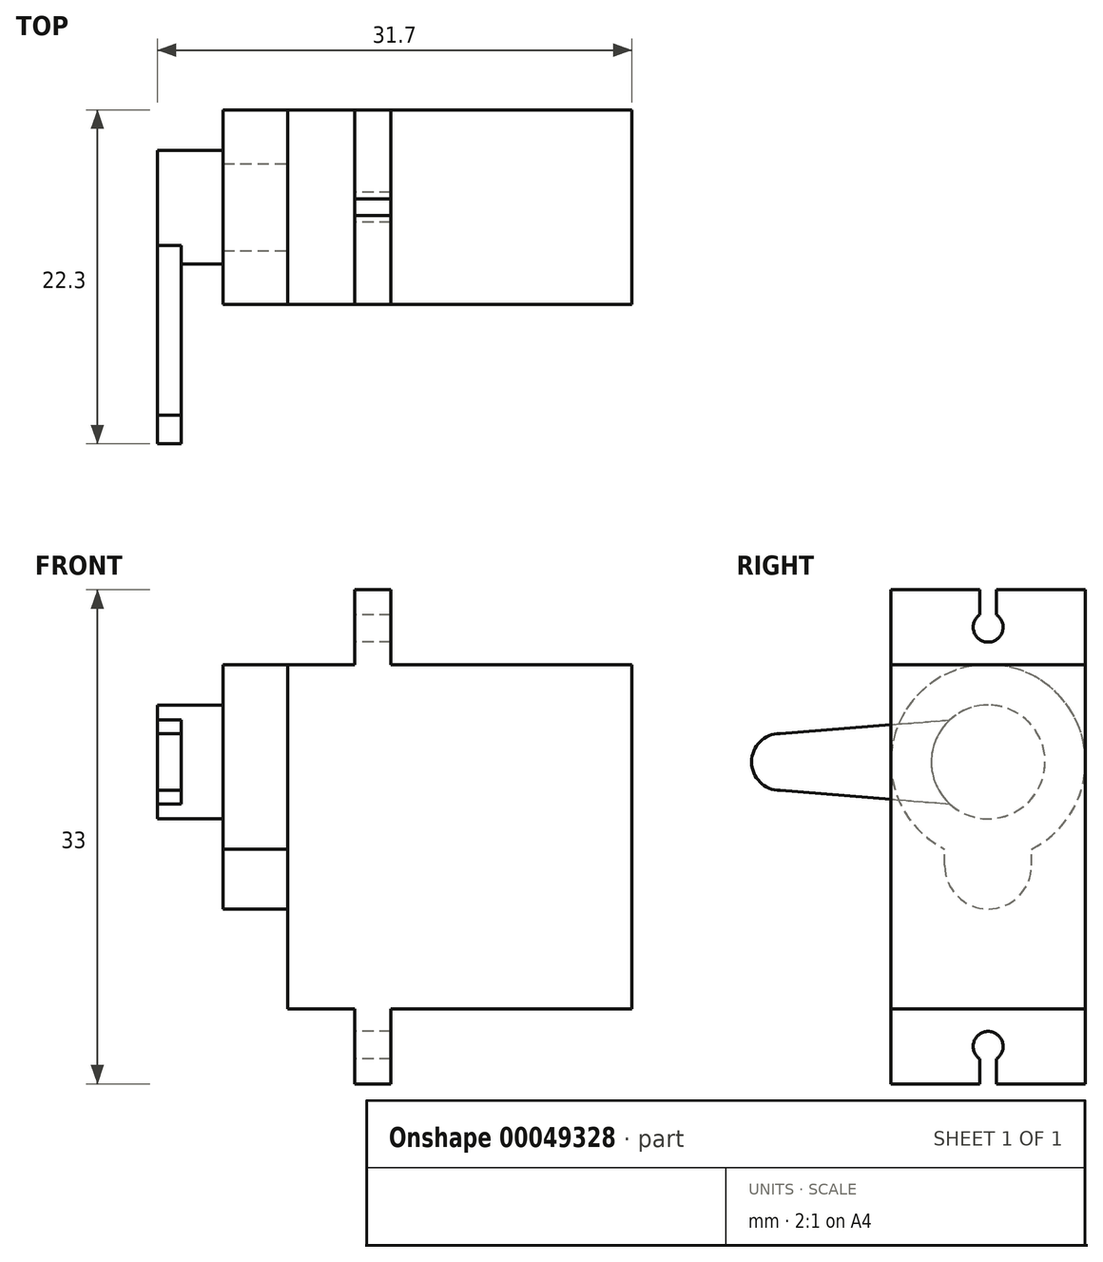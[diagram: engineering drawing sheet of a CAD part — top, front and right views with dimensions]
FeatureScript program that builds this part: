
annotation { "Feature Type Name" : "Feature", "Feature Type Description" : "" }
export const myFeature = defineFeature(function(context is Context, id is Id, definition is map)
    precondition{}
    {
        {
            var Q0;
            Q0=qCreatedBy(makeId("Front.planeOp"),FACE);
            var sketch = newSketch(context, id + "F0", { "sketchPlane" : qUnion([Q0])});
            skLineSegment(sketch, "E0.bottom", {"start": v(-23, 11.5) * mm, "end": v(0, 11.5) * mm});
            skLineSegment(sketch, "E0.top", {"start": v(-23, -11.5) * mm, "end": v(0, -11.5) * mm});
            skLineSegment(sketch, "E0.left", {"start": v(-23, 11.5) * mm, "end": v(-23, -11.5) * mm});
            skLineSegment(sketch, "E0.right", {"start": v(0, 11.5) * mm, "end": v(0, -11.5) * mm});
            skLineSegment(sketch, "E1.bottom", {"start": v(-18.5, 16.5) * mm, "end": v(-16.1, 16.5) * mm});
            skLineSegment(sketch, "E1.top", {"start": v(-18.5, -16.5) * mm, "end": v(-16.1, -16.5) * mm});
            skLineSegment(sketch, "E1.left", {"start": v(-18.5, 16.5) * mm, "end": v(-18.5, -16.5) * mm});
            skLineSegment(sketch, "E1.right", {"start": v(-16.1, 16.5) * mm, "end": v(-16.1, -16.5) * mm});
            skLineSegment(sketch, "E2", {"start": v(-23, 0) * mm, "end": v(0, 0) * mm, "construction": true});
            skSolve(sketch);
        }
        {
            var Q0;
            {var subQ5=sQuery(id+"F0.wireOp",EDGE,"E0.left");Q0=makeQuery(id+"F0.imprint","IMPRINT",FACE,{"disambiguationData":[TD([[makeQuery(id+"F0.imprint","IMPRINT",EDGE,{"derivedFrom":subQ5}),1.0]])]});}
            var Q1;
            {var subQ3=sQuery(id+"F0.wireOp",EDGE,"E1.bottom");Q1=makeQuery(id+"F0.imprint","IMPRINT",FACE,{"disambiguationData":[TD([[makeQuery(id+"F0.imprint","IMPRINT",EDGE,{"derivedFrom":subQ3}),-1.0]])]});}
            var Q2;
            {var subQ5=sQuery(id+"F0.wireOp",EDGE,"E0.right");Q2=makeQuery(id+"F0.imprint","IMPRINT",FACE,{"disambiguationData":[TD([[makeQuery(id+"F0.imprint","IMPRINT",EDGE,{"derivedFrom":subQ5}),-1.0]])]});}
            var Q3;
            {var subQ3=sQuery(id+"F0.wireOp",EDGE,"E1.top");Q3=makeQuery(id+"F0.imprint","IMPRINT",FACE,{"disambiguationData":[TD([[makeQuery(id+"F0.imprint","IMPRINT",EDGE,{"derivedFrom":subQ3}),1.0]])]});}
            var Q4;
            {var subQ3=sQuery(id+"F0.wireOp",EDGE,"E0.bottom");var subQ5=sQuery(id+"F0.wireOp",EDGE,"E1.left");var subQ7=makeQuery(id+"F0.imprint","INTERSECT",VERTEX,{"derivedFrom":[subQ3,subQ5]});Q4=makeQuery(id+"F0.imprint","IMPRINT",FACE,{"disambiguationData":[TD([[makeQuery(id+"F0.imprint","IMPRINT",EDGE,{"disambiguationData":[TD([[subQ7,-1.0]])],"derivedFrom":subQ3}),-1.0]])]});}
            extrude(context, id + "F1", {"entities" : qUnion([Q0, Q1, Q2, Q3, Q4]), "depth" : 13 * mm});
        }
        {
            var Q0;
            Q0=makeQuery(id+"F1.opExtrude","SWEPT_FACE",FACE,{"disambiguationData":[OSD([sQuery(id+"F0.wireOp",EDGE,"E0.left")])]});
            var sketch = newSketch(context, id + "F2", { "sketchPlane" : qUnion([Q0])});
            skLineSegment(sketch, "E3", {"start": v(6.5, 11.5) * mm, "end": v(6.5, -11.5) * mm, "construction": true});
            skArc(sketch, "E4", {"start": v(9.4, -0.82) * mm, "mid": v(6.5, 11.5) * mm, "end": v(3.6, -0.82) * mm});
            skArc(sketch, "E5", {"start": v(3.6, -1.92) * mm, "mid": v(6.5, -4.82) * mm, "end": v(9.4, -1.92) * mm});
            skLineSegment(sketch, "E6", {"start": v(9.4, -1.92) * mm, "end": v(9.4, -0.82) * mm});
            skLineSegment(sketch, "E7", {"start": v(3.6, -1.92) * mm, "end": v(3.6, -0.82) * mm});
            skLineSegment(sketch, "E8", {"start": v(6.5, -4.82) * mm, "end": v(0, -4.82) * mm, "construction": true});
            skLineSegment(sketch, "E9", {"start": v(6.5, -4.82) * mm, "end": v(13, -4.82) * mm, "construction": true});
            skSolve(sketch);
        }
        {
            var Q0;
            Q0=makeQuery(id+"F2.imprint","IMPRINT",FACE,{"disambiguationData":[TD([[makeQuery(id+"F2.imprint","IMPRINT",EDGE,{"derivedFrom":sQuery(id+"F2.wireOp",EDGE,"E5")}),1.0]])]});
            extrude(context, id + "F3", {"entities" : qUnion([Q0]), "operationType" : NewBodyOperationType.ADD, "depth" : 4.3 * mm});
        }
        {
            var Q0;
            {var subQ0=sQuery(id+"F0.wireOp",EDGE,"E1.left");Q0=makeQuery(id+"F1.opExtrude","SWEPT_FACE",FACE,{"disambiguationData":[OSD([subQ0]),TDD([makeQuery(id+"F0.imprint","IMPRINT",EDGE,{"disambiguationData":[TD([[makeQuery(id+"F0.imprint","INTERSECT",VERTEX,{"derivedFrom":[sQuery(id+"F0.wireOp",EDGE,"E1.top"),subQ0]}),1.0]])],"derivedFrom":subQ0})])]});}
            var sketch = newSketch(context, id + "F4", { "sketchPlane" : qUnion([Q0])});
            skLineSegment(sketch, "E10", {"start": v(6.5, -16.5) * mm, "end": v(6.5, 16.5) * mm, "construction": true});
            skLineSegment(sketch, "E11", {"start": v(13, 0) * mm, "end": v(0, 0) * mm, "construction": true});
            skArc(sketch, "E12", {"start": v(7.05, -14.84) * mm, "mid": v(6.5, -13) * mm, "end": v(5.95, -14.84) * mm});
            skLineSegment(sketch, "E13.top", {"start": v(5.95, -16.5) * mm, "end": v(7.05, -16.5) * mm});
            skLineSegment(sketch, "E13.left", {"start": v(5.95, -14.84) * mm, "end": v(5.95, -16.5) * mm});
            skLineSegment(sketch, "E13.right", {"start": v(7.05, -14.84) * mm, "end": v(7.05, -16.5) * mm});
            skLineSegment(sketch, "E14.MirrorCS", {"start": v(5.95, 14.84) * mm, "end": v(5.95, 16.5) * mm});
            skLineSegment(sketch, "E15.MirrorCS", {"start": v(5.95, 16.5) * mm, "end": v(7.05, 16.5) * mm});
            skLineSegment(sketch, "E16.MirrorCS", {"start": v(7.05, 14.84) * mm, "end": v(7.05, 16.5) * mm});
            skArc(sketch, "E17.MirrorCS", {"start": v(7.05, 14.84) * mm, "mid": v(6.5, 13) * mm, "end": v(5.95, 14.84) * mm});
            skSolve(sketch);
        }
        {
            var Q0;
            Q0=makeQuery(id+"F4.imprint","IMPRINT",FACE,{"disambiguationData":[TD([[makeQuery(id+"F4.imprint","IMPRINT",EDGE,{"derivedFrom":sQuery(id+"F4.wireOp",EDGE,"E14.MirrorCS")}),-1.0]])]});
            var Q1;
            Q1=makeQuery(id+"F4.imprint","IMPRINT",FACE,{"disambiguationData":[TD([[makeQuery(id+"F4.imprint","IMPRINT",EDGE,{"derivedFrom":sQuery(id+"F4.wireOp",EDGE,"E12")}),1.0]])]});
            extrude(context, id + "F5", {"entities" : qUnion([Q0, Q1]), "operationType" : NewBodyOperationType.REMOVE, "endBound" : BoundingType.THROUGH_ALL, "oppositeDirection" : true, "depth" : 25 * mm});
        }
        {
            var Q0;
            Q0=makeQuery(id+"F3.opExtrude","CAP_FACE",FACE,{"disambiguationData":[OSD([sQuery(id+"F2.wireOp",EDGE,"E4"),sQuery(id+"F2.wireOp",EDGE,"E5"),sQuery(id+"F2.wireOp",EDGE,"E6"),sQuery(id+"F2.wireOp",EDGE,"E7")])],"isStart":false});
            var sketch = newSketch(context, id + "F6", { "sketchPlane" : qUnion([Q0])});
            skLineSegment(sketch, "E18", {"start": v(0, 5) * mm, "end": v(13, 5) * mm, "construction": true});
            skCircle(sketch, "E19", {"center": v(6.5, 5) * mm, "radius": 3.8 * mm});
            skSolve(sketch);
        }
        {
            var Q0;
            Q0=makeQuery(id+"F6.imprint","IMPRINT",FACE,{"disambiguationData":[TD([[makeQuery(id+"F6.imprint","IMPRINT",EDGE,{"derivedFrom":sQuery(id+"F6.wireOp",EDGE,"E19")}),1.0]])]});
            extrude(context, id + "F7", {"entities" : qUnion([Q0]), "depth" : 4.4 * mm});
        }
        {
            var Q0;
            Q0=makeQuery(id+"F7.opExtrude","CAP_FACE",FACE,{"disambiguationData":[OSD([sQuery(id+"F6.wireOp",EDGE,"E19")])],"isStart":false});
            var sketch = newSketch(context, id + "F8", { "sketchPlane" : qUnion([Q0])});
            skLineSegment(sketch, "E20", {"start": v(6.5, 5) * mm, "end": v(2.7, 5) * mm, "construction": true});
            skLineSegment(sketch, "E21", {"start": v(6.5, 5) * mm, "end": v(22.3, 5) * mm, "construction": true});
            skCircle(sketch, "E22", {"center": v(20.4, 5) * mm, "radius": 1.9 * mm});
            skLineSegment(sketch, "E23", {"start": v(20.4, 6.9) * mm, "end": v(9.07, 7.8) * mm});
            skLineSegment(sketch, "E24.MirrorCS", {"start": v(20.4, 3.1) * mm, "end": v(9.07, 2.2) * mm});
            skLineSegment(sketch, "E25.MirrorCS", {"start": v(20.4, 6.9) * mm, "end": v(9.07, 7.8) * mm, "construction": true});
            skSolve(sketch);
        }
        {
            var Q0;
            {var subQ2=sQuery(id+"F8.wireOp",EDGE,"E23");Q0=makeQuery(id+"F8.imprint","IMPRINT",FACE,{"disambiguationData":[TD([[makeQuery(id+"F8.imprint","IMPRINT",EDGE,{"derivedFrom":subQ2}),1.0]])]});}
            var Q1;
            {var subQ0=sQuery(id+"F8.wireOp",EDGE,"E22");var subQ2=makeQuery(id+"F8.imprint","INTERSECT",VERTEX,{"derivedFrom":[subQ0,sQuery(id+"F8.wireOp",EDGE,"E23")]});Q1=makeQuery(id+"F8.imprint","IMPRINT",FACE,{"disambiguationData":[TD([[makeQuery(id+"F8.imprint","IMPRINT",EDGE,{"disambiguationData":[TD([[subQ2,-1.0]])],"derivedFrom":subQ0}),1.0]])]});}
            extrude(context, id + "F9", {"entities" : qUnion([Q0, Q1]), "operationType" : NewBodyOperationType.ADD, "oppositeDirection" : true, "depth" : 1.6 * mm});
        }
    });
